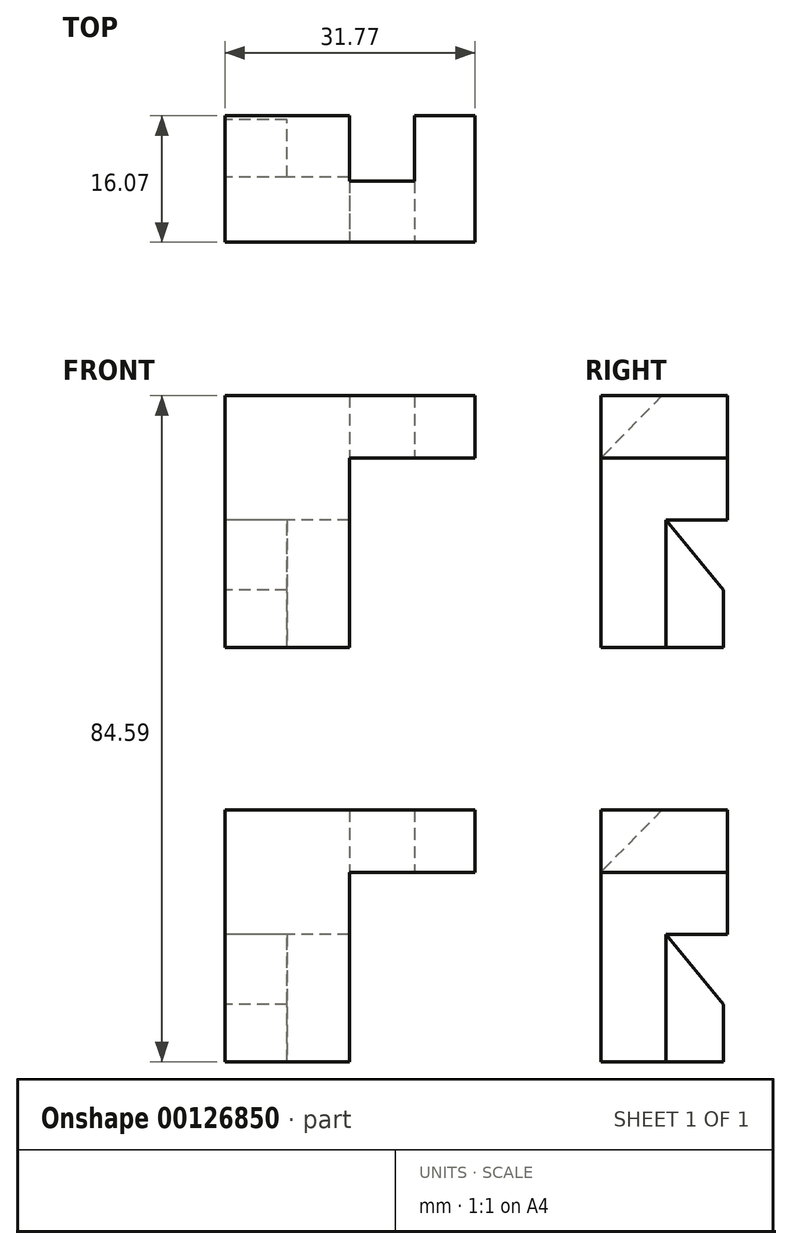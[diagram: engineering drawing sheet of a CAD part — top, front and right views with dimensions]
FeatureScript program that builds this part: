
annotation { "Feature Type Name" : "Feature", "Feature Type Description" : "" }
export const myFeature = defineFeature(function(context is Context, id is Id, definition is map)
    precondition{}
    {
        {
            var Q0;
            Q0=qCreatedBy(makeId("Front.planeOp"),FACE);
            var sketch = newSketch(context, id + "F0", { "sketchPlane" : qUnion([Q0])});
            skLineSegment(sketch, "E0.bottom", {"start": v(7.9, 7.9) * mm, "end": v(-7.9, 7.9) * mm});
            skLineSegment(sketch, "E0.top", {"start": v(7.9, -7.9) * mm, "end": v(-7.9, -7.9) * mm});
            skLineSegment(sketch, "E0.left", {"start": v(7.9, 7.9) * mm, "end": v(7.9, -7.9) * mm});
            skLineSegment(sketch, "E0.right", {"start": v(-7.9, 7.9) * mm, "end": v(-7.9, -7.9) * mm});
            skPoint(sketch, "E0.middle", {"position": v(0, 0) * mm});
            skSolve(sketch);
        }
        {
            var Q0;
            Q0=makeQuery(id+"F0.imprint","IMPRINT",FACE,{"disambiguationData":[TD([[makeQuery(id+"F0.imprint","IMPRINT",EDGE,{"derivedFrom":sQuery(id+"F0.wireOp",EDGE,"E0.bottom")}),1.0]])]});
            extrude(context, id + "F1", {"entities" : qUnion([Q0]), "oppositeDirection" : true, "depth" : 16.07 * mm});
        }
        {
            var Q0;
            Q0=makeQuery(id+"F1.opExtrude","SWEPT_FACE",FACE,{"disambiguationData":[OSD([sQuery(id+"F0.wireOp",EDGE,"E0.left")])]});
            var sketch = newSketch(context, id + "F2", { "sketchPlane" : qUnion([Q0])});
            skLineSegment(sketch, "E1", {"start": v(0, 7.9) * mm, "end": v(7.76, 7.9) * mm});
            skLineSegment(sketch, "E2", {"start": v(0, 7.9) * mm, "end": v(0, 0.15) * mm});
            skLineSegment(sketch, "E3", {"start": v(7.76, 7.9) * mm, "end": v(0, 0) * mm});
            skSolve(sketch);
        }
        {
            var Q0;
            Q0=makeQuery(id+"F2.imprint","IMPRINT",FACE,{"disambiguationData":[TD([[makeQuery(id+"F2.imprint","IMPRINT",EDGE,{"derivedFrom":sQuery(id+"F2.wireOp",EDGE,"E1")}),1.0]])]});
            extrude(context, id + "F3", {"entities" : qUnion([Q0]), "operationType" : NewBodyOperationType.ADD, "depth" : 8.27 * mm});
        }
        {
            var Q0;
            Q0=makeQuery(id+"F3.opExtrude","CAP_FACE",FACE,{"disambiguationData":[OSD([sQuery(id+"F0.wireOp",EDGE,"E0.left"),sQuery(id+"F2.wireOp",EDGE,"E1"),sQuery(id+"F2.wireOp",EDGE,"E2"),sQuery(id+"F2.wireOp",EDGE,"E3")])],"isStart":false});
            var sketch = newSketch(context, id + "F4", { "sketchPlane" : qUnion([Q0])});
            skLineSegment(sketch, "E4.0", {"start": v(16.07, 7.9) * mm, "end": v(16.07, -7.9) * mm});
            skLineSegment(sketch, "E5.bottom", {"start": v(0, 7.9) * mm, "end": v(16.07, 7.9) * mm});
            skLineSegment(sketch, "E5.top", {"start": v(0, 0) * mm, "end": v(16.07, 0) * mm});
            skLineSegment(sketch, "E5.left", {"start": v(0, 7.9) * mm, "end": v(0, 0) * mm});
            skLineSegment(sketch, "E5.right", {"start": v(16.07, 7.9) * mm, "end": v(16.07, 0) * mm});
            skSolve(sketch);
        }
        {
            var Q0;
            {var subQ0=sQuery(id+"F4.wireOp",EDGE,"E5.left");Q0=makeQuery(id+"F4.imprint","IMPRINT",FACE,{"disambiguationData":[TD([[makeQuery(id+"F4.imprint","IMPRINT",EDGE,{"derivedFrom":subQ0}),1.0]])]});}
            var Q1;
            Q1=makeQuery(id+"F4.imprint","IMPRINT",FACE,{"disambiguationData":[TD([[makeQuery(id+"F4.imprint","IMPRINT",EDGE,{"derivedFrom":sQuery(id+"F4.wireOp",EDGE,"E5.top")}),1.0]])]});
            extrude(context, id + "F5", {"entities" : qUnion([Q0, Q1]), "operationType" : NewBodyOperationType.ADD, "depth" : 7.68 * mm});
        }
        {
            var Q0;
            {var subQ0=sQuery(id+"F0.wireOp",EDGE,"E0.left");Q0=makeQuery(id+"F5.boolean.opBoolean","MERGE",FACE,{"derivedFrom":[makeQuery(id+"F3.boolean.opBoolean","MERGE",FACE,{"derivedFrom":[makeQuery(id+"F1.opExtrude","CAP_FACE",FACE,{"disambiguationData":[OSD([sQuery(id+"F0.wireOp",EDGE,"E0.bottom"),sQuery(id+"F0.wireOp",EDGE,"E0.top"),subQ0,sQuery(id+"F0.wireOp",EDGE,"E0.right")])],"isStart":true}),makeQuery(id+"F3.opExtrude","SWEPT_FACE",FACE,{"disambiguationData":[OSD([subQ0,sQuery(id+"F2.wireOp",EDGE,"E2")])]})]}),makeQuery(id+"F5.opExtrude","SWEPT_FACE",FACE,{"disambiguationData":[OSD([sQuery(id+"F4.wireOp",EDGE,"E5.left")])]})]});}
            var sketch = newSketch(context, id + "F6", { "sketchPlane" : qUnion([Q0])});
            skLineSegment(sketch, "E6.bottom", {"start": v(-7.9, -7.9) * mm, "end": v(7.9, -7.9) * mm});
            skLineSegment(sketch, "E6.top", {"start": v(-7.9, -24.07) * mm, "end": v(7.9, -24.07) * mm});
            skLineSegment(sketch, "E6.left", {"start": v(-7.9, -7.9) * mm, "end": v(-7.9, -24.07) * mm});
            skLineSegment(sketch, "E6.right", {"start": v(7.9, -7.9) * mm, "end": v(7.9, -24.07) * mm});
            skSolve(sketch);
        }
        {
            var Q0;
            Q0 = qSketchRegion(id + "F6", true);
            extrude(context, id + "F7", {"entities" : qUnion([Q0]), "operationType" : NewBodyOperationType.ADD, "oppositeDirection" : true, "depth" : 8.26 * mm});
        }
        {
            var Q0;
            Q0=makeQuery(id+"F7.boolean.opBoolean","MERGE",FACE,{"derivedFrom":[makeQuery(id+"F1.opExtrude","SWEPT_FACE",FACE,{"disambiguationData":[OSD([sQuery(id+"F0.wireOp",EDGE,"E0.right")])]}),makeQuery(id+"F7.opExtrude","SWEPT_FACE",FACE,{"disambiguationData":[OSD([sQuery(id+"F6.wireOp",EDGE,"E6.left")])]})]});
            var sketch = newSketch(context, id + "F8", { "sketchPlane" : qUnion([Q0])});
            skLineSegment(sketch, "E7", {"start": v(-8.26, -24.07) * mm, "end": v(-15.56, -24.07) * mm});
            skLineSegment(sketch, "E8", {"start": v(-15.56, -24.07) * mm, "end": v(-15.56, -16.77) * mm});
            skLineSegment(sketch, "E9", {"start": v(-15.56, -16.77) * mm, "end": v(-8.26, -7.9) * mm});
            skSolve(sketch);
        }
        {
            var Q0;
            Q0=makeQuery(id+"F8.imprint","IMPRINT",FACE,{"disambiguationData":[TD([[makeQuery(id+"F8.imprint","IMPRINT",EDGE,{"derivedFrom":sQuery(id+"F8.wireOp",EDGE,"E7")}),-1.0]])]});
            extrude(context, id + "F9", {"entities" : qUnion([Q0]), "operationType" : NewBodyOperationType.ADD, "oppositeDirection" : true, "depth" : 7.89 * mm});
        }
        {
            var Q0;
            Q0=makeQuery(id+"F1.opExtrude","SWEPT_BODY",BODY,{"disambiguationData":[OSD([sQuery(id+"F0.wireOp",EDGE,"E0.bottom"),sQuery(id+"F0.wireOp",EDGE,"E0.top"),sQuery(id+"F0.wireOp",EDGE,"E0.left"),sQuery(id+"F0.wireOp",EDGE,"E0.right")])]});
            transform(context, id + "F10", {"entities" : qUnion([Q0]), "transformType" : TransformType.TRANSLATION_3D, "dx" : 0 * mm, "dy" : 0 * mm, "dz" : 52.6 * mm, "makeCopy" : true});
        }
    });
